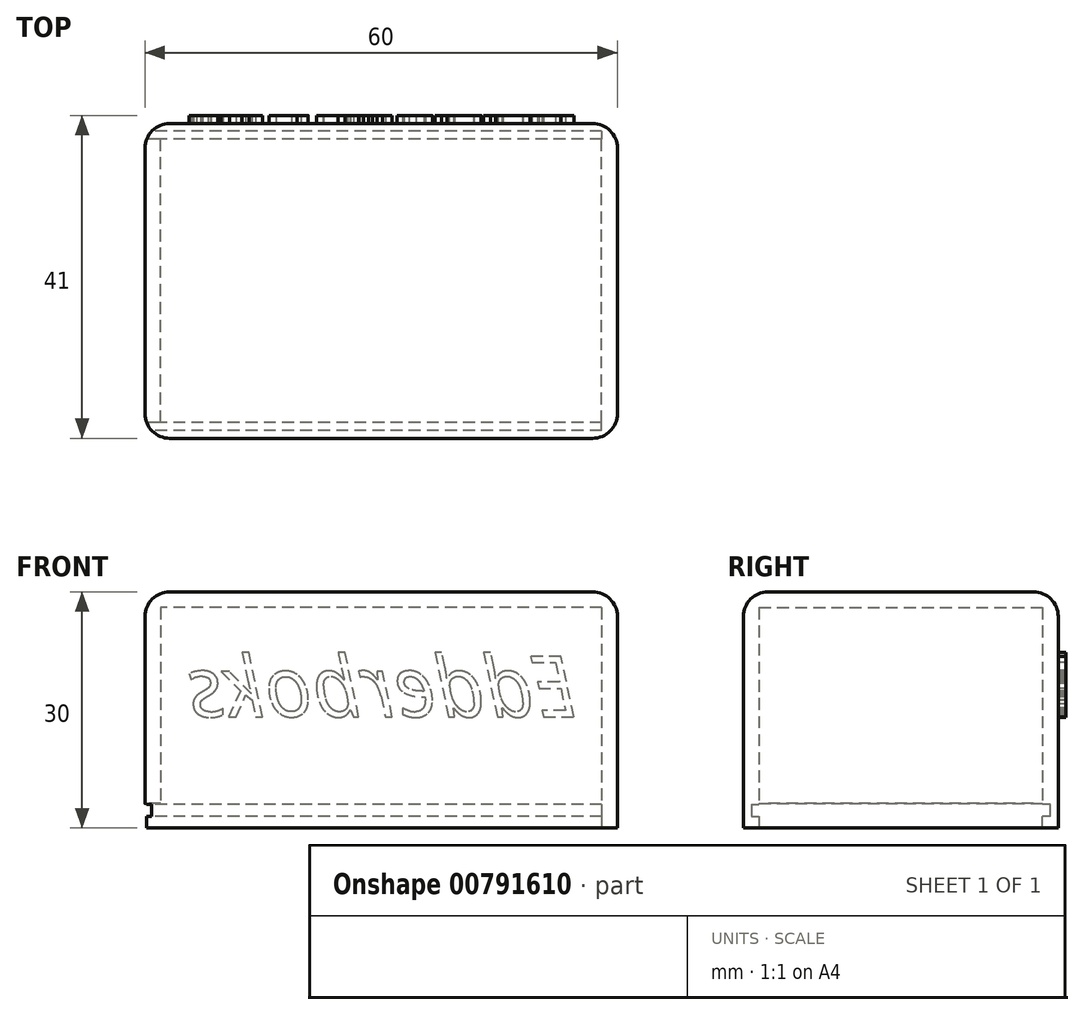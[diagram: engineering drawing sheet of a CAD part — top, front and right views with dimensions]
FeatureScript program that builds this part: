
annotation { "Feature Type Name" : "Feature", "Feature Type Description" : "" }
export const myFeature = defineFeature(function(context is Context, id is Id, definition is map)
    precondition{}
    {
        {
            var Q0;
            Q0=qCreatedBy(makeId("Top.planeOp"),FACE);
            var sketch = newSketch(context, id + "F0", { "sketchPlane" : qUnion([Q0])});
            skLineSegment(sketch, "E0.bottom", {"start": v(30, -20) * mm, "end": v(-30, -20) * mm});
            skLineSegment(sketch, "E0.top", {"start": v(30, 20) * mm, "end": v(-30, 20) * mm});
            skLineSegment(sketch, "E0.left", {"start": v(30, -20) * mm, "end": v(30, 20) * mm});
            skLineSegment(sketch, "E0.right", {"start": v(-30, -20) * mm, "end": v(-30, 20) * mm});
            skPoint(sketch, "E0.middle", {"position": v(0, 0) * mm});
            skLineSegment(sketch, "E1.bottom", {"start": v(28, -18) * mm, "end": v(-28, -18) * mm});
            skLineSegment(sketch, "E1.top", {"start": v(28, 18) * mm, "end": v(-28, 18) * mm});
            skLineSegment(sketch, "E1.left", {"start": v(28, -18) * mm, "end": v(28, 18) * mm});
            skLineSegment(sketch, "E1.right", {"start": v(-28, -18) * mm, "end": v(-28, 18) * mm});
            skSolve(sketch);
        }
        {
            var Q0;
            Q0=makeQuery(id+"F0.imprint","IMPRINT",FACE,{"disambiguationData":[TD([[makeQuery(id+"F0.imprint","IMPRINT",EDGE,{"derivedFrom":sQuery(id+"F0.wireOp",EDGE,"E0.bottom")}),-1.0]])]});
            var Q1;
            Q1=makeQuery(id+"F0.imprint","IMPRINT",FACE,{"disambiguationData":[TD([[makeQuery(id+"F0.imprint","IMPRINT",EDGE,{"derivedFrom":sQuery(id+"F0.wireOp",EDGE,"E1.bottom")}),-1.0]])]});
            extrude(context, id + "F1", {"entities" : qUnion([Q0, Q1]), "depth" : 30 * mm, "offsetDistance" : 25 * mm});
        }
        {
            var Q0;
            Q0=makeQuery(id+"F0.imprint","IMPRINT",FACE,{"disambiguationData":[TD([[makeQuery(id+"F0.imprint","IMPRINT",EDGE,{"derivedFrom":sQuery(id+"F0.wireOp",EDGE,"E1.bottom")}),-1.0]])]});
            extrude(context, id + "F2", {"entities" : qUnion([Q0]), "operationType" : NewBodyOperationType.REMOVE, "depth" : 28 * mm, "offsetDistance" : 25 * mm});
        }
        {
            var Q0;
            Q0=makeQuery(id+"F1.opExtrude","SWEPT_EDGE",EDGE,{"disambiguationData":[OSD([sQuery(id+"F0.wireOp",EDGE,"E0.bottom"),sQuery(id+"F0.wireOp",EDGE,"E0.left")])]});
            var Q1;
            Q1=makeQuery(id+"F1.opExtrude","CAP_EDGE",EDGE,{"disambiguationData":[OSD([sQuery(id+"F0.wireOp",EDGE,"E0.left")])],"isStart":false});
            var Q2;
            Q2=makeQuery(id+"F1.opExtrude","SWEPT_EDGE",EDGE,{"disambiguationData":[OSD([sQuery(id+"F0.wireOp",EDGE,"E0.top"),sQuery(id+"F0.wireOp",EDGE,"E0.left")])]});
            var Q3;
            Q3=makeQuery(id+"F1.opExtrude","CAP_EDGE",EDGE,{"disambiguationData":[OSD([sQuery(id+"F0.wireOp",EDGE,"E0.top")])],"isStart":false});
            var Q4;
            Q4=makeQuery(id+"F1.opExtrude","SWEPT_EDGE",EDGE,{"disambiguationData":[OSD([sQuery(id+"F0.wireOp",EDGE,"E0.top"),sQuery(id+"F0.wireOp",EDGE,"E0.right")])]});
            var Q5;
            Q5=makeQuery(id+"F1.opExtrude","CAP_EDGE",EDGE,{"disambiguationData":[OSD([sQuery(id+"F0.wireOp",EDGE,"E0.right")])],"isStart":false});
            var Q6;
            Q6=makeQuery(id+"F1.opExtrude","SWEPT_EDGE",EDGE,{"disambiguationData":[OSD([sQuery(id+"F0.wireOp",EDGE,"E0.bottom"),sQuery(id+"F0.wireOp",EDGE,"E0.right")])]});
            var Q7;
            Q7=makeQuery(id+"F1.opExtrude","CAP_EDGE",EDGE,{"disambiguationData":[OSD([sQuery(id+"F0.wireOp",EDGE,"E0.bottom")])],"isStart":false});
            fillet(context, id + "F3", {"entities" : qUnion([Q0, Q1, Q2, Q3, Q4, Q5, Q6, Q7]), "radius" : 3.14 * mm, "tangentPropagation" : true, "allowEdgeOverflow" : false});
        }
        {
            var Q0;
            Q0=makeQuery(id+"F1.opExtrude","SWEPT_FACE",FACE,{"disambiguationData":[OSD([sQuery(id+"F0.wireOp",EDGE,"E0.top")])]});
            var sketch = newSketch(context, id + "F4", { "sketchPlane" : qUnion([Q0])});
            skText(sketch, "E2", { "text": "Edderboks", "fontName": "OpenSans-Italic.ttf"});
            const initialGuessF4  = {"E2": [-0.02492, 0.01413, 1, 0, 0.00774]};
            skSetInitialGuess(sketch, initialGuessF4);
            skSolve(sketch);
        }
        {
            var Q0;
            Q0=makeQuery(id+"F2.boolean.opBoolean","COPY",FACE,{"derivedFrom":makeQuery(id+"F2.opExtrude","SWEPT_FACE",FACE,{"disambiguationData":[OSD([sQuery(id+"F0.wireOp",EDGE,"E1.top")])]})});
            var sketch = newSketch(context, id + "F5", { "sketchPlane" : qUnion([Q0])});
            skLineSegment(sketch, "E3.bottom", {"start": v(-28, 28) * mm, "end": v(28, 28) * mm, "construction": true});
            skLineSegment(sketch, "E3.top", {"start": v(-28, 0) * mm, "end": v(28, 0) * mm, "construction": true});
            skLineSegment(sketch, "E3.left", {"start": v(-28, 28) * mm, "end": v(-28, 0) * mm, "construction": true});
            skLineSegment(sketch, "E3.right", {"start": v(28, 28) * mm, "end": v(28, 0) * mm, "construction": true});
            skLineSegment(sketch, "E4.bottom", {"start": v(28, 3) * mm, "end": v(-30, 3) * mm});
            skLineSegment(sketch, "E4.top", {"start": v(28, 1.5) * mm, "end": v(-30, 1.5) * mm});
            skLineSegment(sketch, "E4.left", {"start": v(28, 3) * mm, "end": v(28, 1.5) * mm});
            skLineSegment(sketch, "E4.right", {"start": v(-30, 3) * mm, "end": v(-30, 1.5) * mm});
            skSolve(sketch);
        }
        {
            var Q0;
            Q0=makeQuery(id+"F2.boolean.opBoolean","COPY",FACE,{"derivedFrom":makeQuery(id+"F2.opExtrude","SWEPT_FACE",FACE,{"disambiguationData":[OSD([sQuery(id+"F0.wireOp",EDGE,"E1.bottom")])]})});
            var sketch = newSketch(context, id + "F6", { "sketchPlane" : qUnion([Q0])});
            skLineSegment(sketch, "E5.bottom", {"start": v(-28, 28) * mm, "end": v(28, 28) * mm, "construction": true});
            skLineSegment(sketch, "E5.top", {"start": v(-28, 0) * mm, "end": v(28, 0) * mm, "construction": true});
            skLineSegment(sketch, "E5.left", {"start": v(-28, 28) * mm, "end": v(-28, 0) * mm, "construction": true});
            skLineSegment(sketch, "E5.right", {"start": v(28, 28) * mm, "end": v(28, 0) * mm, "construction": true});
            skLineSegment(sketch, "E6.bottom", {"start": v(-28, 3) * mm, "end": v(30, 3) * mm});
            skLineSegment(sketch, "E6.top", {"start": v(-28, 1.5) * mm, "end": v(30, 1.5) * mm});
            skLineSegment(sketch, "E6.left", {"start": v(-28, 3) * mm, "end": v(-28, 1.5) * mm});
            skLineSegment(sketch, "E6.right", {"start": v(30, 3) * mm, "end": v(30, 1.5) * mm});
            skSolve(sketch);
        }
        {
            var Q0;
            {var subQ0=sQuery(id+"F6.wireOp",EDGE,"E6.left");Q0=makeQuery(id+"F6.imprint","IMPRINT",FACE,{"disambiguationData":[TD([[makeQuery(id+"F6.imprint","IMPRINT",EDGE,{"derivedFrom":subQ0}),1.0]])]});}
            extrude(context, id + "F7", {"entities" : qUnion([Q0]), "operationType" : NewBodyOperationType.REMOVE, "oppositeDirection" : true, "depth" : 1 * mm, "offsetDistance" : 25 * mm});
        }
        {
            var Q0;
            {var subQ0=sQuery(id+"F5.wireOp",EDGE,"E4.left");Q0=makeQuery(id+"F5.imprint","IMPRINT",FACE,{"disambiguationData":[TD([[makeQuery(id+"F5.imprint","IMPRINT",EDGE,{"derivedFrom":subQ0}),-1.0]])]});}
            extrude(context, id + "F8", {"entities" : qUnion([Q0]), "operationType" : NewBodyOperationType.REMOVE, "oppositeDirection" : true, "depth" : 1 * mm, "offsetDistance" : 25 * mm});
        }
        {
            var Q0;
            Q0=makeQuery(id+"F1.opExtrude","CAP_FACE",FACE,{"disambiguationData":[OSD([sQuery(id+"F0.wireOp",EDGE,"E0.bottom"),sQuery(id+"F0.wireOp",EDGE,"E0.top"),sQuery(id+"F0.wireOp",EDGE,"E0.left"),sQuery(id+"F0.wireOp",EDGE,"E0.right")])],"isStart":true});
            var sketch = newSketch(context, id + "F9", { "sketchPlane" : qUnion([Q0])});
            skLineSegment(sketch, "E7.bottom", {"start": v(-28, -18) * mm, "end": v(-30, -18) * mm});
            skLineSegment(sketch, "E7.top", {"start": v(-28, 18) * mm, "end": v(-30, 18) * mm});
            skLineSegment(sketch, "E7.left", {"start": v(-28, -18) * mm, "end": v(-28, 18) * mm});
            skLineSegment(sketch, "E7.right", {"start": v(-30, -18) * mm, "end": v(-30, 18) * mm});
            skSolve(sketch);
        }
        {
            var Q0;
            Q0 = qSketchRegion(id + "F9", true);
            extrude(context, id + "F10", {"entities" : qUnion([Q0]), "operationType" : NewBodyOperationType.REMOVE, "oppositeDirection" : true, "depth" : 3.1 * mm, "offsetDistance" : 25 * mm});
        }
        {
            var Q0;
            {var subQ0=sQuery(id+"F6.wireOp",EDGE,"E6.right");Q0=makeQuery(id+"F6.imprint","IMPRINT",FACE,{"disambiguationData":[TD([[makeQuery(id+"F6.imprint","IMPRINT",EDGE,{"derivedFrom":subQ0}),-1.0]])]});}
            extrude(context, id + "F11", {"entities" : qUnion([Q0]), "operationType" : NewBodyOperationType.REMOVE, "depth" : -1 * mm, "offsetDistance" : 25 * mm});
        }
        {
            var Q0;
            {var subQ0=sQuery(id+"F5.wireOp",EDGE,"E4.right");Q0=makeQuery(id+"F5.imprint","IMPRINT",FACE,{"disambiguationData":[TD([[makeQuery(id+"F5.imprint","IMPRINT",EDGE,{"derivedFrom":subQ0}),1.0]])]});}
            extrude(context, id + "F12", {"entities" : qUnion([Q0]), "operationType" : NewBodyOperationType.REMOVE, "oppositeDirection" : true, "depth" : 1 * mm, "offsetDistance" : 25 * mm});
        }
        {
            var Q0;
            Q0 = qSketchRegion(id + "F4", true);
            extrude(context, id + "F13", {"entities" : qUnion([Q0]), "operationType" : NewBodyOperationType.ADD, "depth" : 1 * mm, "offsetDistance" : 25 * mm});
        }
    });
